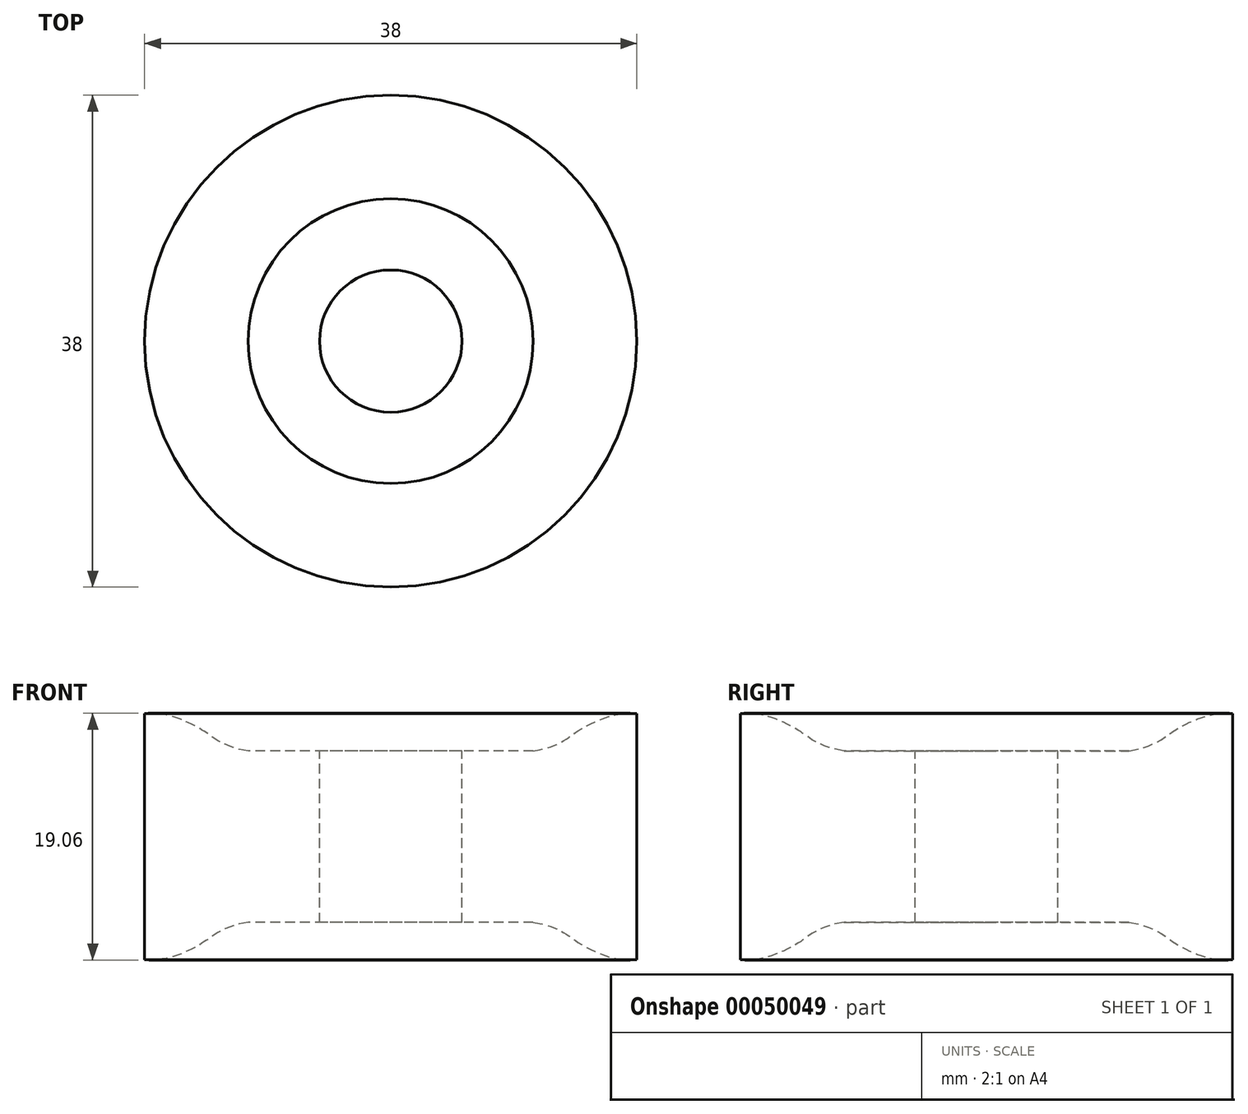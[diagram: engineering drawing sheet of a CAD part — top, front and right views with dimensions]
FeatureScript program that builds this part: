
annotation { "Feature Type Name" : "Feature", "Feature Type Description" : "" }
export const myFeature = defineFeature(function(context is Context, id is Id, definition is map)
    precondition{}
    {
        {
            var Q0;
            Q0=qCreatedBy(makeId("Front.planeOp"),FACE);
            var sketch = newSketch(context, id + "F0", { "sketchPlane" : qUnion([Q0])});
            skLineSegment(sketch, "E0", {"start": v(0, 13.04) * mm, "end": v(0, -14) * mm, "construction": true});
            skLineSegment(sketch, "E1", {"start": v(5.5, 6.62) * mm, "end": v(5.5, -6.62) * mm});
            skLineSegment(sketch, "E2", {"start": v(5.5, -6.62) * mm, "end": v(11, -6.62) * mm});
            skLineSegment(sketch, "E3", {"start": v(19, -9.5) * mm, "end": v(19, 9.5) * mm});
            skLineSegment(sketch, "E4", {"start": v(11, 6.62) * mm, "end": v(5.5, 6.62) * mm});
            skLineSegment(sketch, "E5", {"start": v(0, 0) * mm, "end": v(5.5, 0) * mm, "construction": true});
            skLineSegment(sketch, "E6", {"start": v(5.5, 0) * mm, "end": v(19, 0) * mm, "construction": true});
            skFitSpline(sketch, "E7", {"points": [v(11, 6.62) * mm, v(13.82, 7.72) * mm, v(14.27, 8.05) * mm, v(19, 9.5) * mm], "startDerivative": vector(12.01, 1.48) * mm, "endDerivative": vector(12.77, -1.53) * mm});
            skFitSpline(sketch, "E8", {"points": [v(11, -6.62) * mm, v(13.82, -7.72) * mm, v(14.27, -8.05) * mm, v(19, -9.5) * mm], "startDerivative": vector(12.01, -1.48) * mm, "endDerivative": vector(12.77, 1.53) * mm});
            skLineSegment(sketch, "E9", {"start": v(14.27, 8.05) * mm, "end": v(14.27, -8.05) * mm, "construction": true});
            skPoint(sketch, "E10", {"position": v(14.27, 0) * mm});
            skPoint(sketch, "E11", {"position": v(13.82, 0) * mm});
            skLineSegment(sketch, "E12", {"start": v(17, 9.74) * mm, "end": v(17, -9.74) * mm, "construction": true});
            skPoint(sketch, "E13", {"position": v(12.48, 0) * mm});
            skPoint(sketch, "E14", {"position": v(17, 0) * mm});
            skLineSegment(sketch, "E15", {"start": v(13.82, 7.72) * mm, "end": v(13.82, -7.72) * mm, "construction": true});
            skLineSegment(sketch, "E16", {"start": v(12.48, 6.8) * mm, "end": v(12.48, -6.8) * mm, "construction": true});
            skSolve(sketch);
        }
        {
            var Q0;
            Q0=qSketchRegion(id+"F0",true);
            var Q1;
            Q1=sQuery(id+"F0.wireOp",EDGE,"E0");
            revolve(context, id + "F1", {"entities" : qUnion([Q0]), "axis" : qUnion([Q1]), "revolveType" : RevolveType.FULL});
        }
    });
